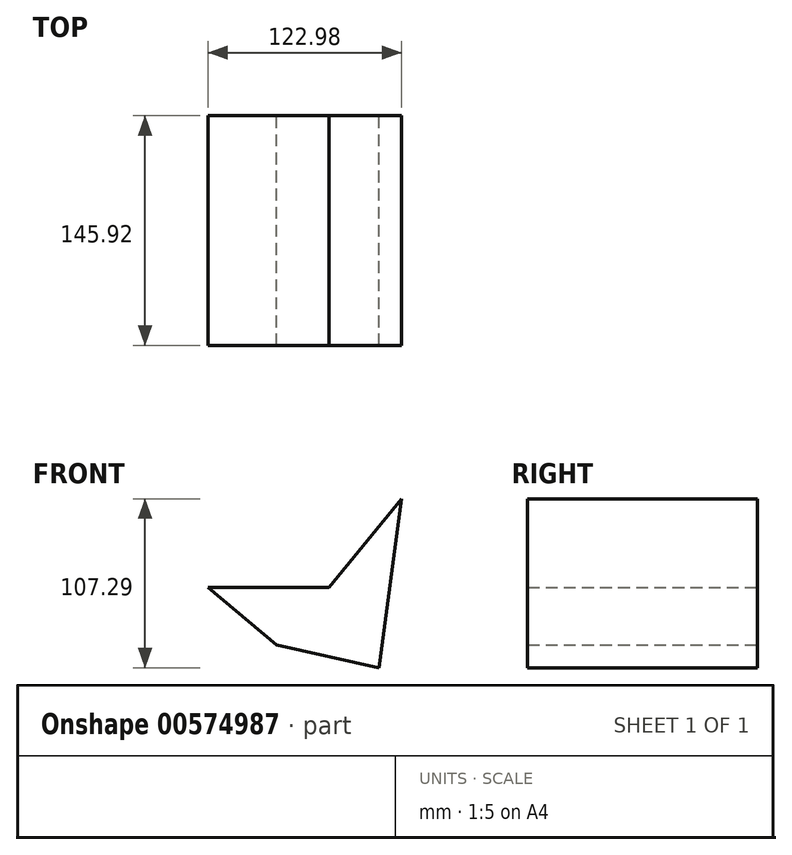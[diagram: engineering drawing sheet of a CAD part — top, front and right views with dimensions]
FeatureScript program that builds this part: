
annotation { "Feature Type Name" : "Feature", "Feature Type Description" : "" }
export const myFeature = defineFeature(function(context is Context, id is Id, definition is map)
    precondition{}
    {
        {
            var Q0;
            Q0=qCreatedBy(makeId("Front.planeOp"),FACE);
            var sketch = newSketch(context, id + "F0", { "sketchPlane" : qUnion([Q0])});
            skLineSegment(sketch, "E0", {"start": v(46.17, 56.36) * mm, "end": v(0, 0) * mm});
            skLineSegment(sketch, "E1", {"start": v(0, 0) * mm, "end": v(46.17, 56.36) * mm});
            skLineSegment(sketch, "E2", {"start": v(31.62, -50.93) * mm, "end": v(46.17, 56.36) * mm});
            skLineSegment(sketch, "E3", {"start": v(31.62, -50.93) * mm, "end": v(-33.27, -36.27) * mm});
            skLineSegment(sketch, "E4", {"start": v(-33.27, -36.27) * mm, "end": v(-76.81, 0) * mm});
            skLineSegment(sketch, "E5", {"start": v(-76.81, 0) * mm, "end": v(0, 0) * mm});
            skSolve(sketch);
        }
        {
            var Q0;
            Q0 = qSketchRegion(id + "F0", true);
            extrude(context, id + "F1", {"entities" : qUnion([Q0]), "depth" : 145.92 * mm, "offsetDistance" : 25.4 * mm});
        }
    });
